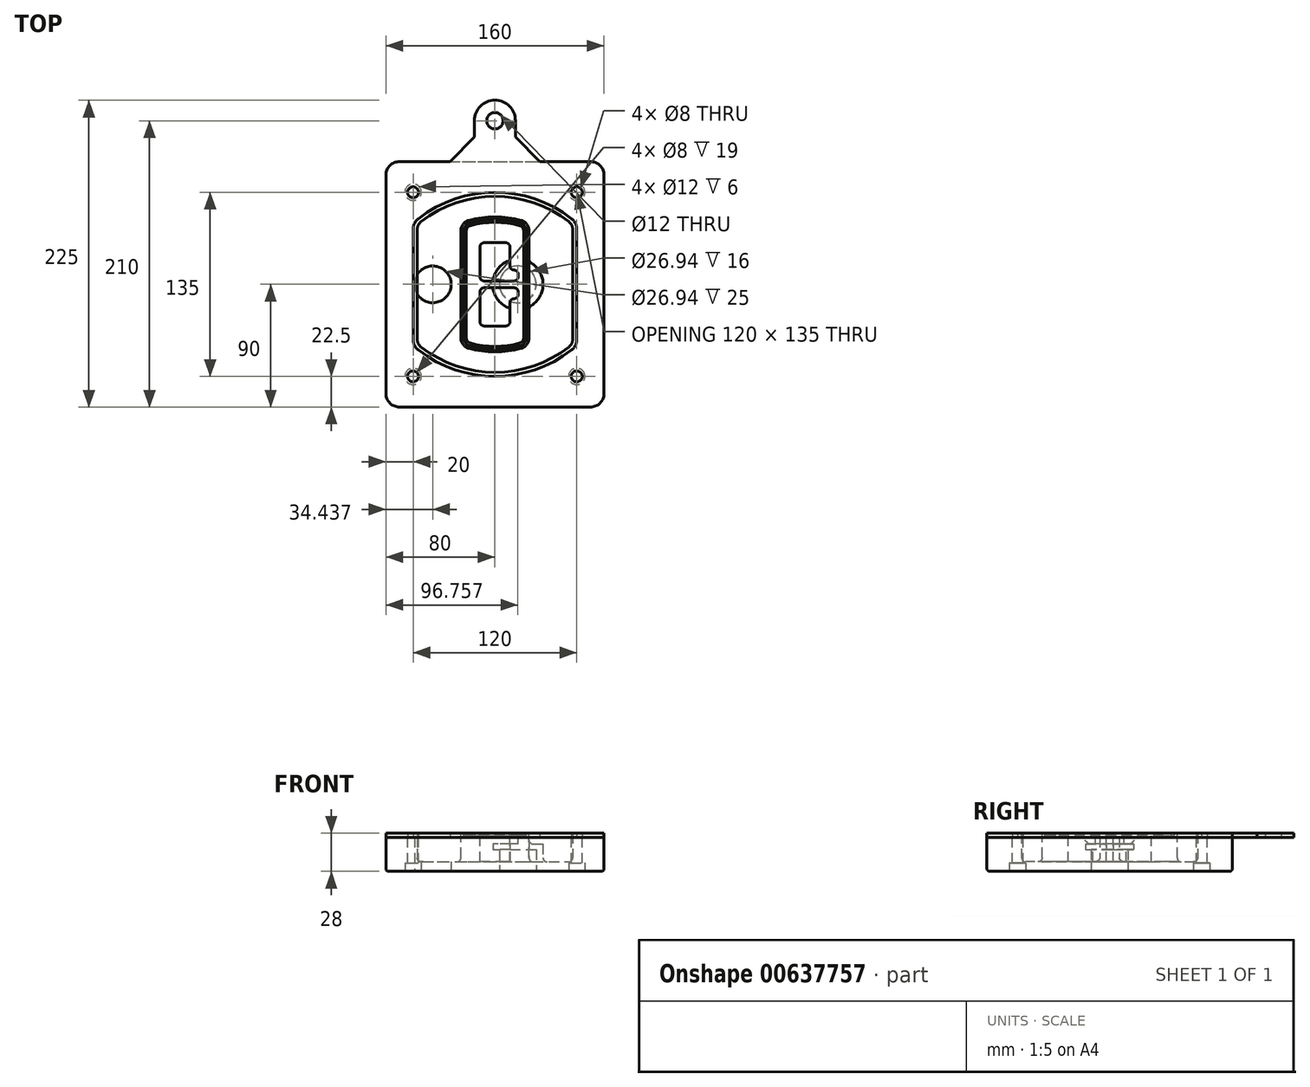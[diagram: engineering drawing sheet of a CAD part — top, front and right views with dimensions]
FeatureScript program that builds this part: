
annotation { "Feature Type Name" : "Feature", "Feature Type Description" : "" }
export const myFeature = defineFeature(function(context is Context, id is Id, definition is map)
    precondition{}
    {
        {
            var Q0;
            Q0=qCreatedBy(makeId("Top.planeOp"),FACE);
            var sketch = newSketch(context, id + "F0", { "sketchPlane" : qUnion([Q0])});
            skPoint(sketch, "E0.rect.middle", {"position": v(0, 0) * mm});
            skLineSegment(sketch, "E1.bottom", {"start": v(-70, -90) * mm, "end": v(70, -90) * mm});
            skLineSegment(sketch, "E1.top", {"start": v(-70, 90) * mm, "end": v(70, 90) * mm});
            skLineSegment(sketch, "E1.left", {"start": v(-80, -80) * mm, "end": v(-80, 80) * mm});
            skLineSegment(sketch, "E1.right", {"start": v(80, -80) * mm, "end": v(80, 80) * mm});
            skLineSegment(sketch, "E2", {"start": v(-80, 90) * mm, "end": v(80, -90) * mm, "construction": true});
            skLineSegment(sketch, "E3", {"start": v(80, 90) * mm, "end": v(-80, -90) * mm, "construction": true});
            skCircle(sketch, "E4", {"center": v(-60, 67.5) * mm, "radius": 4 * mm});
            skCircle(sketch, "E5", {"center": v(60, 67.5) * mm, "radius": 4 * mm});
            skCircle(sketch, "E6", {"center": v(60, -67.5) * mm, "radius": 4 * mm});
            skCircle(sketch, "E7", {"center": v(-60, -67.5) * mm, "radius": 4 * mm});
            skLineSegment(sketch, "E8", {"start": v(-60, 67.5) * mm, "end": v(60, 67.5) * mm, "construction": true});
            skLineSegment(sketch, "E9", {"start": v(60, 67.5) * mm, "end": v(60, -67.5) * mm, "construction": true});
            skLineSegment(sketch, "E10", {"start": v(60, -67.5) * mm, "end": v(-60, -67.5) * mm, "construction": true});
            skLineSegment(sketch, "E11", {"start": v(-60, -67.5) * mm, "end": v(-60, 67.5) * mm, "construction": true});
            skLineSegment(sketch, "E12", {"start": v(-60, 40.3) * mm, "end": v(-60, -40.3) * mm});
            skLineSegment(sketch, "E13", {"start": v(60, 40.3) * mm, "end": v(60, -40.3) * mm});
            skArc(sketch, "E14", {"start": v(56.15, 48.18) * mm, "mid": v(0, 67.5) * mm, "end": v(-56.15, 48.18) * mm});
            skArc(sketch, "E15", {"start": v(-56.15, -48.18) * mm, "mid": v(0, -67.5) * mm, "end": v(56.15, -48.18) * mm});
            skLineSegment(sketch, "E16", {"start": v(-60, 0) * mm, "end": v(60, 0) * mm, "construction": true});
            skPoint(sketch, "E17.visualSharp", {"position": v(-60, -45) * mm});
            skArc(sketch, "E17.filletArc", {"start": v(-60, -40.3) * mm, "mid": v(-58.99, -44.68) * mm, "end": v(-56.15, -48.18) * mm});
            skPoint(sketch, "E18.visualSharp", {"position": v(-60, 45) * mm});
            skArc(sketch, "E18.filletArc", {"start": v(-56.15, 48.18) * mm, "mid": v(-58.99, 44.68) * mm, "end": v(-60, 40.3) * mm});
            skPoint(sketch, "E19.visualSharp", {"position": v(60, 45) * mm});
            skArc(sketch, "E19.filletArc", {"start": v(60, 40.3) * mm, "mid": v(58.99, 44.68) * mm, "end": v(56.15, 48.18) * mm});
            skPoint(sketch, "E20.visualSharp", {"position": v(60, -45) * mm});
            skArc(sketch, "E20.filletArc", {"start": v(56.15, -48.18) * mm, "mid": v(58.99, -44.68) * mm, "end": v(60, -40.3) * mm});
            skPoint(sketch, "E21.visualSharp", {"position": v(-80, 90) * mm});
            skArc(sketch, "E21.filletArc", {"start": v(-70, 90) * mm, "mid": v(-77.07, 87.07) * mm, "end": v(-80, 80) * mm});
            skPoint(sketch, "E22.visualSharp", {"position": v(80, 90) * mm});
            skArc(sketch, "E22.filletArc", {"start": v(80, 80) * mm, "mid": v(77.07, 87.07) * mm, "end": v(70, 90) * mm});
            skPoint(sketch, "E23.visualSharp", {"position": v(80, -90) * mm});
            skArc(sketch, "E23.filletArc", {"start": v(70, -90) * mm, "mid": v(77.07, -87.07) * mm, "end": v(80, -80) * mm});
            skPoint(sketch, "E24.visualSharp", {"position": v(-80, -90) * mm});
            skArc(sketch, "E24.filletArc", {"start": v(-80, -80) * mm, "mid": v(-77.07, -87.07) * mm, "end": v(-70, -90) * mm});
            skArc(sketch, "E25.0", {"start": v(57, 40.3) * mm, "mid": v(56.3, 43.36) * mm, "end": v(54.3, 45.81) * mm});
            skLineSegment(sketch, "E25.1", {"start": v(57, 40.3) * mm, "end": v(57, -40.3) * mm});
            skArc(sketch, "E25.2", {"start": v(54.3, -45.81) * mm, "mid": v(56.3, -43.36) * mm, "end": v(57, -40.3) * mm});
            skArc(sketch, "E25.3", {"start": v(-54.3, -45.81) * mm, "mid": v(0, -64.5) * mm, "end": v(54.3, -45.81) * mm});
            skArc(sketch, "E25.4", {"start": v(-57, -40.3) * mm, "mid": v(-56.3, -43.36) * mm, "end": v(-54.3, -45.81) * mm});
            skArc(sketch, "E25.5", {"start": v(54.3, 45.81) * mm, "mid": v(0, 64.5) * mm, "end": v(-54.3, 45.81) * mm});
            skLineSegment(sketch, "E25.6", {"start": v(-57, 40.3) * mm, "end": v(-57, -40.3) * mm});
            skArc(sketch, "E25.7", {"start": v(-54.3, 45.81) * mm, "mid": v(-56.3, 43.36) * mm, "end": v(-57, 40.3) * mm});
            skArc(sketch, "E26.0", {"start": v(-58.62, 51.33) * mm, "mid": v(-62.58, 46.43) * mm, "end": v(-64, 40.3) * mm});
            skArc(sketch, "E26.1", {"start": v(58.62, 51.33) * mm, "mid": v(0, 71.5) * mm, "end": v(-58.62, 51.33) * mm});
            skArc(sketch, "E26.2", {"start": v(64, 40.3) * mm, "mid": v(62.58, 46.43) * mm, "end": v(58.62, 51.33) * mm});
            skLineSegment(sketch, "E26.3", {"start": v(64, 40.3) * mm, "end": v(64, -40.3) * mm});
            skArc(sketch, "E26.4", {"start": v(58.62, -51.33) * mm, "mid": v(62.58, -46.43) * mm, "end": v(64, -40.3) * mm});
            skLineSegment(sketch, "E26.5", {"start": v(-64, 40.3) * mm, "end": v(-64, -40.3) * mm});
            skArc(sketch, "E26.6", {"start": v(-58.62, -51.33) * mm, "mid": v(0, -71.5) * mm, "end": v(58.62, -51.33) * mm});
            skArc(sketch, "E26.7", {"start": v(-64, -40.3) * mm, "mid": v(-62.58, -46.43) * mm, "end": v(-58.62, -51.33) * mm});
            skSolve(sketch);
        }
        {
            var Q0;
            Q0=makeQuery(id+"F0.imprint","IMPRINT",FACE,{"disambiguationData":[TD([[makeQuery(id+"F0.imprint","IMPRINT",EDGE,{"derivedFrom":sQuery(id+"F0.wireOp",EDGE,"E1.bottom")}),1.0]])]});
            var Q1;
            Q1=makeQuery(id+"F0.imprint","IMPRINT",FACE,{"disambiguationData":[TD([[makeQuery(id+"F0.imprint","IMPRINT",EDGE,{"derivedFrom":sQuery(id+"F0.wireOp",EDGE,"E12")}),1.0]])]});
            var Q2;
            Q2=makeQuery(id+"F0.imprint","IMPRINT",FACE,{"disambiguationData":[TD([[makeQuery(id+"F0.imprint","IMPRINT",EDGE,{"derivedFrom":sQuery(id+"F0.wireOp",EDGE,"E25.0")}),1.0]])]});
            var Q3;
            Q3=makeQuery(id+"F0.imprint","IMPRINT",FACE,{"disambiguationData":[TD([[makeQuery(id+"F0.imprint","IMPRINT",EDGE,{"derivedFrom":sQuery(id+"F0.wireOp",EDGE,"E12")}),-1.0]])]});
            extrude(context, id + "F1", {"entities" : qUnion([Q0, Q1, Q2, Q3]), "oppositeDirection" : true, "depth" : 25 * mm});
        }
        {
            var Q0;
            Q0=makeQuery(id+"F0.imprint","IMPRINT",FACE,{"disambiguationData":[TD([[makeQuery(id+"F0.imprint","IMPRINT",EDGE,{"derivedFrom":sQuery(id+"F0.wireOp",EDGE,"E12")}),1.0]])]});
            extrude(context, id + "F2", {"entities" : qUnion([Q0]), "operationType" : NewBodyOperationType.ADD, "depth" : 3 * mm});
        }
        {
            var Q0;
            Q0=makeQuery(id+"F0.imprint","IMPRINT",FACE,{"disambiguationData":[TD([[makeQuery(id+"F0.imprint","IMPRINT",EDGE,{"derivedFrom":sQuery(id+"F0.wireOp",EDGE,"E25.0")}),1.0]])]});
            extrude(context, id + "F3", {"entities" : qUnion([Q0]), "operationType" : NewBodyOperationType.REMOVE, "oppositeDirection" : true, "depth" : 18 * mm});
        }
        {
            var Q0;
            Q0=makeQuery(id+"F2.opExtrude","CAP_FACE",FACE,{"disambiguationData":[OSD([sQuery(id+"F0.wireOp",EDGE,"E12"),sQuery(id+"F0.wireOp",EDGE,"E13"),sQuery(id+"F0.wireOp",EDGE,"E14"),sQuery(id+"F0.wireOp",EDGE,"E15"),sQuery(id+"F0.wireOp",EDGE,"E17.filletArc"),sQuery(id+"F0.wireOp",EDGE,"E18.filletArc"),sQuery(id+"F0.wireOp",EDGE,"E19.filletArc"),sQuery(id+"F0.wireOp",EDGE,"E20.filletArc"),sQuery(id+"F0.wireOp",EDGE,"E25.0"),sQuery(id+"F0.wireOp",EDGE,"E25.1"),sQuery(id+"F0.wireOp",EDGE,"E25.2"),sQuery(id+"F0.wireOp",EDGE,"E25.3"),sQuery(id+"F0.wireOp",EDGE,"E25.4"),sQuery(id+"F0.wireOp",EDGE,"E25.5"),sQuery(id+"F0.wireOp",EDGE,"E25.6"),sQuery(id+"F0.wireOp",EDGE,"E25.7")])],"isStart":false});
            var sketch = newSketch(context, id + "F4", { "sketchPlane" : qUnion([Q0])});
            skArc(sketch, "E27.0", {"start": v(-19.08, -46.97) * mm, "mid": v(0, -49.5) * mm, "end": v(19.08, -46.97) * mm});
            skArc(sketch, "E28.0", {"start": v(19.08, 46.97) * mm, "mid": v(0, 49.5) * mm, "end": v(-19.08, 46.97) * mm});
            skLineSegment(sketch, "E29", {"start": v(-25, 39.25) * mm, "end": v(-25, -39.25) * mm});
            skLineSegment(sketch, "E30", {"start": v(25, 39.25) * mm, "end": v(25, -39.25) * mm});
            skLineSegment(sketch, "E31", {"start": v(-25, 45.1) * mm, "end": v(25, 45.1) * mm, "construction": true});
            skLineSegment(sketch, "E32", {"start": v(-25, -45.1) * mm, "end": v(25, -45.1) * mm, "construction": true});
            skPoint(sketch, "E33.visualSharp", {"position": v(-25, 45.1) * mm});
            skArc(sketch, "E33.filletArc", {"start": v(-19.08, 46.97) * mm, "mid": v(-23.35, 44.11) * mm, "end": v(-25, 39.25) * mm});
            skPoint(sketch, "E34.visualSharp", {"position": v(25, 45.1) * mm});
            skArc(sketch, "E34.filletArc", {"start": v(25, 39.25) * mm, "mid": v(23.35, 44.11) * mm, "end": v(19.08, 46.97) * mm});
            skPoint(sketch, "E35.visualSharp", {"position": v(25, -45.1) * mm});
            skArc(sketch, "E35.filletArc", {"start": v(19.08, -46.97) * mm, "mid": v(23.35, -44.11) * mm, "end": v(25, -39.25) * mm});
            skPoint(sketch, "E36.visualSharp", {"position": v(-25, -45.1) * mm});
            skArc(sketch, "E36.filletArc", {"start": v(-25, -39.25) * mm, "mid": v(-23.35, -44.11) * mm, "end": v(-19.08, -46.97) * mm});
            skArc(sketch, "E37.0", {"start": v(54.3, 45.81) * mm, "mid": v(0, 64.5) * mm, "end": v(-54.3, 45.81) * mm});
            skArc(sketch, "E37.1", {"start": v(-54.3, 45.81) * mm, "mid": v(-56.3, 43.36) * mm, "end": v(-57, 40.3) * mm});
            skLineSegment(sketch, "E37.2", {"start": v(-57, 40.3) * mm, "end": v(-57, -40.3) * mm});
            skArc(sketch, "E37.3", {"start": v(-57, -40.3) * mm, "mid": v(-56.3, -43.36) * mm, "end": v(-54.3, -45.81) * mm});
            skArc(sketch, "E37.4", {"start": v(-54.3, -45.81) * mm, "mid": v(0, -64.5) * mm, "end": v(54.3, -45.81) * mm});
            skArc(sketch, "E37.5", {"start": v(54.3, -45.81) * mm, "mid": v(56.3, -43.36) * mm, "end": v(57, -40.3) * mm});
            skLineSegment(sketch, "E37.6", {"start": v(57, 40.3) * mm, "end": v(57, -40.3) * mm});
            skArc(sketch, "E37.7", {"start": v(57, 40.3) * mm, "mid": v(56.3, 43.36) * mm, "end": v(54.3, 45.81) * mm});
            skLineSegment(sketch, "E38.0", {"start": v(23, 39.25) * mm, "end": v(23, -39.25) * mm});
            skArc(sketch, "E38.1", {"start": v(18.56, -45.04) * mm, "mid": v(21.76, -42.9) * mm, "end": v(23, -39.25) * mm});
            skArc(sketch, "E38.2", {"start": v(-18.56, -45.04) * mm, "mid": v(0, -47.5) * mm, "end": v(18.56, -45.04) * mm});
            skArc(sketch, "E38.3", {"start": v(-23, -39.25) * mm, "mid": v(-21.76, -42.9) * mm, "end": v(-18.56, -45.04) * mm});
            skLineSegment(sketch, "E38.4", {"start": v(-23, 39.25) * mm, "end": v(-23, -39.25) * mm});
            skArc(sketch, "E38.5", {"start": v(23, 39.25) * mm, "mid": v(21.76, 42.9) * mm, "end": v(18.56, 45.04) * mm});
            skArc(sketch, "E38.6", {"start": v(-18.56, 45.04) * mm, "mid": v(-21.76, 42.9) * mm, "end": v(-23, 39.25) * mm});
            skArc(sketch, "E38.7", {"start": v(18.56, 45.04) * mm, "mid": v(0, 47.5) * mm, "end": v(-18.56, 45.04) * mm});
            skArc(sketch, "E39.0", {"start": v(21, 39.25) * mm, "mid": v(20.18, 41.68) * mm, "end": v(18.04, 43.1) * mm});
            skLineSegment(sketch, "E39.1", {"start": v(21, 39.25) * mm, "end": v(21, -39.25) * mm});
            skArc(sketch, "E39.2", {"start": v(18.04, -43.1) * mm, "mid": v(20.18, -41.68) * mm, "end": v(21, -39.25) * mm});
            skArc(sketch, "E39.3", {"start": v(-18.04, -43.1) * mm, "mid": v(0, -45.5) * mm, "end": v(18.04, -43.1) * mm});
            skArc(sketch, "E39.4", {"start": v(-21, -39.25) * mm, "mid": v(-20.18, -41.68) * mm, "end": v(-18.04, -43.1) * mm});
            skArc(sketch, "E39.5", {"start": v(18.04, 43.1) * mm, "mid": v(0, 45.5) * mm, "end": v(-18.04, 43.1) * mm});
            skLineSegment(sketch, "E39.6", {"start": v(-21, 39.25) * mm, "end": v(-21, -39.25) * mm});
            skArc(sketch, "E39.7", {"start": v(-18.04, 43.1) * mm, "mid": v(-20.18, 41.68) * mm, "end": v(-21, 39.25) * mm});
            skLineSegment(sketch, "E40", {"start": v(-25, 0) * mm, "end": v(25, 0) * mm, "construction": true});
            skLineSegment(sketch, "E41", {"start": v(-11, 5.5) * mm, "end": v(-11, 27.5) * mm});
            skLineSegment(sketch, "E42", {"start": v(-8, 30.5) * mm, "end": v(8, 30.5) * mm});
            skLineSegment(sketch, "E43", {"start": v(11, 27.5) * mm, "end": v(11, 13.5) * mm});
            skLineSegment(sketch, "E44", {"start": v(14, 10.5) * mm, "end": v(14, 10.5) * mm});
            skLineSegment(sketch, "E45", {"start": v(17, 7.5) * mm, "end": v(17, 5.5) * mm});
            skLineSegment(sketch, "E46", {"start": v(14, 2.5) * mm, "end": v(-8, 2.5) * mm});
            skPoint(sketch, "E47.visualSharp", {"position": v(-11, 30.5) * mm});
            skArc(sketch, "E47.filletArc", {"start": v(-8, 30.5) * mm, "mid": v(-10.12, 29.62) * mm, "end": v(-11, 27.5) * mm});
            skPoint(sketch, "E48.visualSharp", {"position": v(11, 30.5) * mm});
            skArc(sketch, "E48.filletArc", {"start": v(11, 27.5) * mm, "mid": v(10.12, 29.62) * mm, "end": v(8, 30.5) * mm});
            skPoint(sketch, "E49.visualSharp", {"position": v(11, 10.5) * mm});
            skArc(sketch, "E49.filletArc", {"start": v(11, 13.5) * mm, "mid": v(11.88, 11.38) * mm, "end": v(14, 10.5) * mm});
            skPoint(sketch, "E50.visualSharp", {"position": v(17, 10.5) * mm});
            skArc(sketch, "E50.filletArc", {"start": v(17, 7.5) * mm, "mid": v(16.12, 9.62) * mm, "end": v(14, 10.5) * mm});
            skPoint(sketch, "E51.visualSharp", {"position": v(17, 2.5) * mm});
            skArc(sketch, "E51.filletArc", {"start": v(14, 2.5) * mm, "mid": v(16.12, 3.38) * mm, "end": v(17, 5.5) * mm});
            skPoint(sketch, "E52.visualSharp", {"position": v(-11, 2.5) * mm});
            skArc(sketch, "E52.filletArc", {"start": v(-11, 5.5) * mm, "mid": v(-10.12, 3.38) * mm, "end": v(-8, 2.5) * mm});
            skLineSegment(sketch, "E53.0.MirrorCS", {"start": v(14, -2.5) * mm, "end": v(-8, -2.5) * mm});
            skArc(sketch, "E54.0.MirrorCS", {"start": v(-11, -5.5) * mm, "mid": v(-10.12, -3.38) * mm, "end": v(-8, -2.5) * mm});
            skLineSegment(sketch, "E55.0.MirrorCS", {"start": v(-11, -5.5) * mm, "end": v(-11, -27.5) * mm});
            skArc(sketch, "E56.0.MirrorCS", {"start": v(-8, -30.5) * mm, "mid": v(-10.12, -29.62) * mm, "end": v(-11, -27.5) * mm});
            skLineSegment(sketch, "E57.0.MirrorCS", {"start": v(-8, -30.5) * mm, "end": v(8, -30.5) * mm});
            skArc(sketch, "E58.0.MirrorCS", {"start": v(11, -27.5) * mm, "mid": v(10.12, -29.62) * mm, "end": v(8, -30.5) * mm});
            skLineSegment(sketch, "E59.0.MirrorCS", {"start": v(11, -27.5) * mm, "end": v(11, -13.5) * mm});
            skArc(sketch, "E60.0.MirrorCS", {"start": v(11, -13.5) * mm, "mid": v(11.88, -11.38) * mm, "end": v(14, -10.5) * mm});
            skArc(sketch, "E61.0.MirrorCS", {"start": v(17, -7.5) * mm, "mid": v(16.12, -9.62) * mm, "end": v(14, -10.5) * mm});
            skLineSegment(sketch, "E62.0.MirrorCS", {"start": v(17, -7.5) * mm, "end": v(17, -5.5) * mm});
            skArc(sketch, "E63.0.MirrorCS", {"start": v(14, -2.5) * mm, "mid": v(16.12, -3.38) * mm, "end": v(17, -5.5) * mm});
            skSolve(sketch);
        }
        {
            var Q0;
            Q0=makeQuery(id+"F4.imprint","IMPRINT",FACE,{"disambiguationData":[TD([[makeQuery(id+"F4.imprint","IMPRINT",EDGE,{"derivedFrom":sQuery(id+"F4.wireOp",EDGE,"E27.0")}),1.0]])]});
            var Q1;
            Q1=makeQuery(id+"F4.imprint","IMPRINT",FACE,{"disambiguationData":[TD([[makeQuery(id+"F4.imprint","IMPRINT",EDGE,{"derivedFrom":sQuery(id+"F4.wireOp",EDGE,"E38.0")}),-1.0]])]});
            var Q2;
            Q2=makeQuery(id+"F4.imprint","IMPRINT",FACE,{"disambiguationData":[TD([[makeQuery(id+"F4.imprint","IMPRINT",EDGE,{"derivedFrom":sQuery(id+"F4.wireOp",EDGE,"E39.0")}),1.0]])]});
            extrude(context, id + "F5", {"entities" : qUnion([Q0, Q1, Q2]), "operationType" : NewBodyOperationType.ADD, "endBound" : BoundingType.UP_TO_NEXT, "oppositeDirection" : true, "depth" : 25 * mm});
        }
        {
            var Q0;
            Q0=makeQuery(id+"F4.imprint","IMPRINT",FACE,{"disambiguationData":[TD([[makeQuery(id+"F4.imprint","IMPRINT",EDGE,{"derivedFrom":sQuery(id+"F4.wireOp",EDGE,"E38.0")}),-1.0]])]});
            extrude(context, id + "F6", {"entities" : qUnion([Q0]), "operationType" : NewBodyOperationType.REMOVE, "oppositeDirection" : true, "depth" : 2 * mm});
        }
        {
            var Q0;
            Q0=makeQuery(id+"F1.opExtrude","CAP_FACE",FACE,{"disambiguationData":[OSD([sQuery(id+"F0.wireOp",EDGE,"E1.bottom"),sQuery(id+"F0.wireOp",EDGE,"E1.top"),sQuery(id+"F0.wireOp",EDGE,"E1.left"),sQuery(id+"F0.wireOp",EDGE,"E1.right"),sQuery(id+"F0.wireOp",EDGE,"E4"),sQuery(id+"F0.wireOp",EDGE,"E5"),sQuery(id+"F0.wireOp",EDGE,"E6"),sQuery(id+"F0.wireOp",EDGE,"E7"),sQuery(id+"F0.wireOp",EDGE,"E21.filletArc"),sQuery(id+"F0.wireOp",EDGE,"E22.filletArc"),sQuery(id+"F0.wireOp",EDGE,"E23.filletArc"),sQuery(id+"F0.wireOp",EDGE,"E24.filletArc")])],"isStart":false});
            var sketch = newSketch(context, id + "F7", { "sketchPlane" : qUnion([Q0])});
            skCircle(sketch, "E64", {"center": v(16.76, 0) * mm, "radius": 13.47 * mm});
            skCircle(sketch, "E65", {"center": v(-45.56, 0) * mm, "radius": 13.47 * mm});
            skLineSegment(sketch, "E66", {"start": v(80, 0) * mm, "end": v(-80, 0) * mm});
            skCircle(sketch, "E67", {"center": v(16.76, 0) * mm, "radius": 18.47 * mm});
            skCircle(sketch, "E68", {"center": v(60, -67.5) * mm, "radius": 6 * mm});
            skCircle(sketch, "E69", {"center": v(-60, -67.5) * mm, "radius": 6 * mm});
            skCircle(sketch, "E70", {"center": v(-60, 67.5) * mm, "radius": 6 * mm});
            skCircle(sketch, "E71", {"center": v(60, 67.5) * mm, "radius": 6 * mm});
            skSolve(sketch);
        }
        {
            var Q0;
            {var subQ1=sQuery(id+"F7.wireOp",EDGE,"E66");var subQ4=sQuery(id+"F7.wireOp",EDGE,"E64");var subQ6=makeQuery(id+"F7.imprint","INTERSECT",VERTEX,{"disambiguationData":[OD(0.0)],"derivedFrom":[subQ4,subQ1]});Q0=makeQuery(id+"F7.imprint","IMPRINT",FACE,{"disambiguationData":[TD([[makeQuery(id+"F7.imprint","IMPRINT",EDGE,{"disambiguationData":[TD([[subQ6,-1.0]])],"derivedFrom":subQ4}),-1.0]])]});}
            var Q1;
            {var subQ0=sQuery(id+"F7.wireOp",EDGE,"E66");var subQ1=sQuery(id+"F7.wireOp",EDGE,"E64");var subQ3=makeQuery(id+"F7.imprint","INTERSECT",VERTEX,{"disambiguationData":[OD(0.0)],"derivedFrom":[subQ1,subQ0]});Q1=makeQuery(id+"F7.imprint","IMPRINT",FACE,{"disambiguationData":[TD([[makeQuery(id+"F7.imprint","IMPRINT",EDGE,{"disambiguationData":[TD([[subQ3,-1.0]])],"derivedFrom":subQ1}),1.0]])]});}
            var Q2;
            {var subQ0=sQuery(id+"F7.wireOp",EDGE,"E66");var subQ1=sQuery(id+"F7.wireOp",EDGE,"E64");var subQ3=makeQuery(id+"F7.imprint","INTERSECT",VERTEX,{"disambiguationData":[OD(0.0)],"derivedFrom":[subQ1,subQ0]});Q2=makeQuery(id+"F7.imprint","IMPRINT",FACE,{"disambiguationData":[TD([[makeQuery(id+"F7.imprint","IMPRINT",EDGE,{"disambiguationData":[TD([[subQ3,1.0]])],"derivedFrom":subQ1}),1.0]])]});}
            var Q3;
            {var subQ1=sQuery(id+"F7.wireOp",EDGE,"E66");var subQ4=sQuery(id+"F7.wireOp",EDGE,"E64");var subQ6=makeQuery(id+"F7.imprint","INTERSECT",VERTEX,{"disambiguationData":[OD(0.0)],"derivedFrom":[subQ4,subQ1]});Q3=makeQuery(id+"F7.imprint","IMPRINT",FACE,{"disambiguationData":[TD([[makeQuery(id+"F7.imprint","IMPRINT",EDGE,{"disambiguationData":[TD([[subQ6,1.0]])],"derivedFrom":subQ4}),-1.0]])]});}
            extrude(context, id + "F8", {"entities" : qUnion([Q0, Q1, Q2, Q3]), "operationType" : NewBodyOperationType.ADD, "oppositeDirection" : true, "depth" : 20 * mm});
        }
        {
            var Q0;
            {var subQ0=sQuery(id+"F7.wireOp",EDGE,"E66");var subQ1=sQuery(id+"F7.wireOp",EDGE,"E64");var subQ3=makeQuery(id+"F7.imprint","INTERSECT",VERTEX,{"disambiguationData":[OD(0.0)],"derivedFrom":[subQ1,subQ0]});Q0=makeQuery(id+"F7.imprint","IMPRINT",FACE,{"disambiguationData":[TD([[makeQuery(id+"F7.imprint","IMPRINT",EDGE,{"disambiguationData":[TD([[subQ3,-1.0]])],"derivedFrom":subQ1}),1.0]])]});}
            var Q1;
            {var subQ0=sQuery(id+"F7.wireOp",EDGE,"E66");var subQ1=sQuery(id+"F7.wireOp",EDGE,"E64");var subQ3=makeQuery(id+"F7.imprint","INTERSECT",VERTEX,{"disambiguationData":[OD(0.0)],"derivedFrom":[subQ1,subQ0]});Q1=makeQuery(id+"F7.imprint","IMPRINT",FACE,{"disambiguationData":[TD([[makeQuery(id+"F7.imprint","IMPRINT",EDGE,{"disambiguationData":[TD([[subQ3,1.0]])],"derivedFrom":subQ1}),1.0]])]});}
            extrude(context, id + "F9", {"entities" : qUnion([Q0, Q1]), "operationType" : NewBodyOperationType.REMOVE, "oppositeDirection" : true, "depth" : 16 * mm});
        }
        {
            var Q0;
            {var subQ0=sQuery(id+"F7.wireOp",EDGE,"E66");var subQ1=sQuery(id+"F7.wireOp",EDGE,"E65");var subQ3=makeQuery(id+"F7.imprint","INTERSECT",VERTEX,{"disambiguationData":[OD(0.0)],"derivedFrom":[subQ1,subQ0]});Q0=makeQuery(id+"F7.imprint","IMPRINT",FACE,{"disambiguationData":[TD([[makeQuery(id+"F7.imprint","IMPRINT",EDGE,{"disambiguationData":[TD([[subQ3,-1.0]])],"derivedFrom":subQ1}),1.0]])]});}
            var Q1;
            {var subQ0=sQuery(id+"F7.wireOp",EDGE,"E66");var subQ1=sQuery(id+"F7.wireOp",EDGE,"E65");var subQ3=makeQuery(id+"F7.imprint","INTERSECT",VERTEX,{"disambiguationData":[OD(0.0)],"derivedFrom":[subQ1,subQ0]});Q1=makeQuery(id+"F7.imprint","IMPRINT",FACE,{"disambiguationData":[TD([[makeQuery(id+"F7.imprint","IMPRINT",EDGE,{"disambiguationData":[TD([[subQ3,1.0]])],"derivedFrom":subQ1}),1.0]])]});}
            extrude(context, id + "F10", {"entities" : qUnion([Q0, Q1]), "operationType" : NewBodyOperationType.REMOVE, "oppositeDirection" : true, "depth" : 25 * mm});
        }
        {
            var Q0;
            Q0=makeQuery(id+"F7.imprint","IMPRINT",FACE,{"disambiguationData":[TD([[makeQuery(id+"F7.imprint","IMPRINT",EDGE,{"derivedFrom":sQuery(id+"F7.wireOp",EDGE,"E68")}),1.0]])]});
            var Q1;
            Q1=makeQuery(id+"F7.imprint","IMPRINT",FACE,{"disambiguationData":[TD([[makeQuery(id+"F7.imprint","IMPRINT",EDGE,{"derivedFrom":makeQuery(id+"F1.opExtrude","CAP_EDGE",EDGE,{"disambiguationData":[OSD([sQuery(id+"F0.wireOp",EDGE,"E5")])],"isStart":false})}),-1.0]])]});
            var Q2;
            Q2=makeQuery(id+"F7.imprint","IMPRINT",FACE,{"disambiguationData":[TD([[makeQuery(id+"F7.imprint","IMPRINT",EDGE,{"derivedFrom":sQuery(id+"F7.wireOp",EDGE,"E69")}),1.0]])]});
            var Q3;
            Q3=makeQuery(id+"F7.imprint","IMPRINT",FACE,{"disambiguationData":[TD([[makeQuery(id+"F7.imprint","IMPRINT",EDGE,{"derivedFrom":makeQuery(id+"F1.opExtrude","CAP_EDGE",EDGE,{"disambiguationData":[OSD([sQuery(id+"F0.wireOp",EDGE,"E4")])],"isStart":false})}),-1.0]])]});
            var Q4;
            Q4=makeQuery(id+"F7.imprint","IMPRINT",FACE,{"disambiguationData":[TD([[makeQuery(id+"F7.imprint","IMPRINT",EDGE,{"derivedFrom":sQuery(id+"F7.wireOp",EDGE,"E70")}),1.0]])]});
            var Q5;
            Q5=makeQuery(id+"F7.imprint","IMPRINT",FACE,{"disambiguationData":[TD([[makeQuery(id+"F7.imprint","IMPRINT",EDGE,{"derivedFrom":makeQuery(id+"F1.opExtrude","CAP_EDGE",EDGE,{"disambiguationData":[OSD([sQuery(id+"F0.wireOp",EDGE,"E7")])],"isStart":false})}),-1.0]])]});
            var Q6;
            Q6=makeQuery(id+"F7.imprint","IMPRINT",FACE,{"disambiguationData":[TD([[makeQuery(id+"F7.imprint","IMPRINT",EDGE,{"derivedFrom":sQuery(id+"F7.wireOp",EDGE,"E71")}),1.0]])]});
            var Q7;
            Q7=makeQuery(id+"F7.imprint","IMPRINT",FACE,{"disambiguationData":[TD([[makeQuery(id+"F7.imprint","IMPRINT",EDGE,{"derivedFrom":makeQuery(id+"F1.opExtrude","CAP_EDGE",EDGE,{"disambiguationData":[OSD([sQuery(id+"F0.wireOp",EDGE,"E6")])],"isStart":false})}),-1.0]])]});
            extrude(context, id + "F11", {"entities" : qUnion([Q0, Q1, Q2, Q3, Q4, Q5, Q6, Q7]), "operationType" : NewBodyOperationType.REMOVE, "oppositeDirection" : true, "depth" : 6 * mm});
        }
        {
            var Q0;
            Q0=makeQuery(id+"F9.boolean.opBoolean","COPY",FACE,{"derivedFrom":makeQuery(id+"F9.opExtrude","CAP_FACE",FACE,{"disambiguationData":[OSD([sQuery(id+"F7.wireOp",EDGE,"E64")])],"isStart":false})});
            var sketch = newSketch(context, id + "F12", { "sketchPlane" : qUnion([Q0])});
            skArc(sketch, "E72.0", {"start": v(11, 17.55) * mm, "mid": v(2.57, 11.82) * mm, "end": v(-1.54, 2.5) * mm});
            skArc(sketch, "E72.1", {"start": v(-1.54, -2.5) * mm, "mid": v(2.57, -11.82) * mm, "end": v(11, -17.55) * mm});
            skLineSegment(sketch, "E73", {"start": v(-1.54, -2.5) * mm, "end": v(14, -2.5) * mm});
            skLineSegment(sketch, "E74.0", {"start": v(14, 2.5) * mm, "end": v(-1.54, 2.5) * mm});
            skArc(sketch, "E74.1", {"start": v(14, 2.5) * mm, "mid": v(16.12, 3.38) * mm, "end": v(17, 5.5) * mm});
            skLineSegment(sketch, "E74.2", {"start": v(17, 7.5) * mm, "end": v(17, 5.5) * mm});
            skArc(sketch, "E74.3", {"start": v(17, 7.5) * mm, "mid": v(16.12, 9.62) * mm, "end": v(14, 10.5) * mm});
            skArc(sketch, "E74.4", {"start": v(11, 13.5) * mm, "mid": v(11.88, 11.38) * mm, "end": v(14, 10.5) * mm});
            skLineSegment(sketch, "E74.5", {"start": v(11, 17.55) * mm, "end": v(11, 13.5) * mm});
            skLineSegment(sketch, "E74.7", {"start": v(14, -2.5) * mm, "end": v(-1.54, -2.5) * mm});
            skArc(sketch, "E74.8", {"start": v(14, -2.5) * mm, "mid": v(16.12, -3.38) * mm, "end": v(17, -5.5) * mm});
            skLineSegment(sketch, "E74.9", {"start": v(17, -7.5) * mm, "end": v(17, -5.5) * mm});
            skArc(sketch, "E74.10", {"start": v(17, -7.5) * mm, "mid": v(16.12, -9.62) * mm, "end": v(14, -10.5) * mm});
            skArc(sketch, "E74.11", {"start": v(11, -13.5) * mm, "mid": v(11.88, -11.38) * mm, "end": v(14, -10.5) * mm});
            skLineSegment(sketch, "E74.12", {"start": v(11, -17.55) * mm, "end": v(11, -13.5) * mm});
            skPoint(sketch, "E75.orphan", {"position": v(11, -27.5) * mm});
            skPoint(sketch, "E76.orphan", {"position": v(-8, -2.5) * mm});
            skPoint(sketch, "E77.orphan", {"position": v(-8, 2.5) * mm});
            skPoint(sketch, "E78.orphan", {"position": v(11, 27.5) * mm});
            skSolve(sketch);
        }
        {
            var Q0;
            {var subQ7=sQuery(id+"F12.wireOp",EDGE,"E72.0");var subQ14=sQuery(id+"F12.wireOp",EDGE,"E72.1");var subQ16=sQuery(id+"F12.wireOp",EDGE,"E74.1");var subQ18=sQuery(id+"F12.wireOp",EDGE,"E74.8");Q0=qUnion([makeQuery(id+"F12.imprint","IMPRINT",FACE,{"disambiguationData":[TD([[makeQuery(id+"F12.imprint","IMPRINT",EDGE,{"derivedFrom":subQ7}),1.0]])]}),makeQuery(id+"F12.imprint","IMPRINT",FACE,{"disambiguationData":[TD([[makeQuery(id+"F12.imprint","IMPRINT",EDGE,{"derivedFrom":subQ14}),1.0]])]}),makeQuery(id+"F12.imprint","IMPRINT",FACE,{"disambiguationData":[TD([[makeQuery(id+"F12.imprint","IMPRINT",EDGE,{"derivedFrom":subQ16}),1.0]])]}),makeQuery(id+"F12.imprint","IMPRINT",FACE,{"disambiguationData":[TD([[makeQuery(id+"F12.imprint","IMPRINT",EDGE,{"derivedFrom":subQ18}),-1.0]])]})]);}
            var Q1;
            Q1=makeQuery(id+"F5.boolean.opBoolean","SPLIT",FACE,{"disambiguationData":[TD([makeQuery(id+"F5.opExtrude","SWEPT_FACE",FACE,{"disambiguationData":[OSD([sQuery(id+"F4.wireOp",EDGE,"E41")])]})])],"derivedFrom":makeQuery(id+"F3.boolean.opBoolean","COPY",FACE,{"derivedFrom":makeQuery(id+"F3.opExtrude","CAP_FACE",FACE,{"disambiguationData":[OSD([sQuery(id+"F0.wireOp",EDGE,"E25.0"),sQuery(id+"F0.wireOp",EDGE,"E25.1"),sQuery(id+"F0.wireOp",EDGE,"E25.2"),sQuery(id+"F0.wireOp",EDGE,"E25.3"),sQuery(id+"F0.wireOp",EDGE,"E25.4"),sQuery(id+"F0.wireOp",EDGE,"E25.5"),sQuery(id+"F0.wireOp",EDGE,"E25.6"),sQuery(id+"F0.wireOp",EDGE,"E25.7")])],"isStart":false})})});
            extrude(context, id + "F13", {"entities" : qUnion([Q0]), "operationType" : NewBodyOperationType.REMOVE, "endBound" : BoundingType.UP_TO_SURFACE, "endBoundEntityFace" : qUnion([Q1]), "depth" : 25 * mm});
        }
        {
            var Q0;
            Q0=makeQuery(id+"F3.boolean.opBoolean","COPY",EDGE,{"derivedFrom":makeQuery(id+"F3.opExtrude","CAP_EDGE",EDGE,{"disambiguationData":[OSD([sQuery(id+"F0.wireOp",EDGE,"E25.6")])],"isStart":false})});
            var Q1;
            Q1=makeQuery(id+"F8.boolean.opBoolean","INTERSECT",EDGE,{"derivedFrom":[makeQuery(id+"F5.opExtrude","SWEPT_FACE",FACE,{"disambiguationData":[OSD([sQuery(id+"F4.wireOp",EDGE,"E30")])]}),makeQuery(id+"F8.opExtrude","CAP_FACE",FACE,{"disambiguationData":[OSD([sQuery(id+"F7.wireOp",EDGE,"E67")])],"isStart":false})]});
            var Q2;
            Q2=makeQuery(id+"F8.boolean.opBoolean","INTERSECT",EDGE,{"disambiguationData":[OD(1.0)],"derivedFrom":[makeQuery(id+"F5.opExtrude","SWEPT_FACE",FACE,{"disambiguationData":[OSD([sQuery(id+"F4.wireOp",EDGE,"E30")])]}),makeQuery(id+"F8.opExtrude","SWEPT_FACE",FACE,{"disambiguationData":[OSD([sQuery(id+"F7.wireOp",EDGE,"E67")])]})]});
            var Q3;
            {var subQ0=sQuery(id+"F4.wireOp",EDGE,"E30");Q3=makeQuery(id+"F8.boolean.opBoolean","SPLIT",EDGE,{"disambiguationData":[TD([makeQuery(id+"F5.opExtrude","SWEPT_FACE",FACE,{"disambiguationData":[OSD([sQuery(id+"F4.wireOp",EDGE,"E35.filletArc")])]})])],"derivedFrom":makeQuery(id+"F5.opExtrude","CAP_EDGE",EDGE,{"disambiguationData":[OSD([subQ0])],"isStart":false})});}
            var Q4;
            {var subQ0=sQuery(id+"F0.wireOp",EDGE,"E25.7");var subQ1=sQuery(id+"F0.wireOp",EDGE,"E25.1");var subQ2=sQuery(id+"F0.wireOp",EDGE,"E25.6");var subQ3=sQuery(id+"F0.wireOp",EDGE,"E25.5");var subQ4=sQuery(id+"F0.wireOp",EDGE,"E25.4");var subQ5=sQuery(id+"F0.wireOp",EDGE,"E25.0");var subQ6=sQuery(id+"F0.wireOp",EDGE,"E25.2");var subQ7=sQuery(id+"F0.wireOp",EDGE,"E25.3");Q4=makeQuery(id+"F8.boolean.opBoolean","INTERSECT",EDGE,{"derivedFrom":[makeQuery(id+"F5.boolean.opBoolean","SPLIT",FACE,{"disambiguationData":[TD([makeQuery(id+"F2.opExtrude","SWEPT_FACE",FACE,{"disambiguationData":[OSD([subQ5])]})])],"derivedFrom":makeQuery(id+"F3.boolean.opBoolean","COPY",FACE,{"derivedFrom":makeQuery(id+"F3.opExtrude","CAP_FACE",FACE,{"disambiguationData":[OSD([subQ5,subQ1,subQ6,subQ7,subQ4,subQ3,subQ2,subQ0])],"isStart":false})})}),makeQuery(id+"F8.opExtrude","SWEPT_FACE",FACE,{"disambiguationData":[OSD([sQuery(id+"F7.wireOp",EDGE,"E67")])]})]});}
            var Q5;
            Q5=makeQuery(id+"F8.boolean.opBoolean","INTERSECT",EDGE,{"disambiguationData":[OD(0.0)],"derivedFrom":[makeQuery(id+"F5.opExtrude","SWEPT_FACE",FACE,{"disambiguationData":[OSD([sQuery(id+"F4.wireOp",EDGE,"E30")])]}),makeQuery(id+"F8.opExtrude","SWEPT_FACE",FACE,{"disambiguationData":[OSD([sQuery(id+"F7.wireOp",EDGE,"E67")])]})]});
            fillet(context, id + "F14", {"entities" : qUnion([Q0, Q1, Q2, Q3, Q4, Q5]), "radius" : 3 * mm, "tangentPropagation" : true, "allowEdgeOverflow" : false});
        }
        {
            var Q0;
            Q0=makeQuery(id+"F1.opExtrude","CAP_EDGE",EDGE,{"disambiguationData":[OSD([sQuery(id+"F0.wireOp",EDGE,"E1.bottom")])],"isStart":false});
            fillet(context, id + "F15", {"entities" : qUnion([Q0]), "radius" : 2 * mm, "tangentPropagation" : true, "allowEdgeOverflow" : false});
        }
        {
            var Q0;
            {var subQ0=sQuery(id+"F0.wireOp",EDGE,"E21.filletArc");var subQ1=sQuery(id+"F0.wireOp",EDGE,"E7");var subQ2=sQuery(id+"F0.wireOp",EDGE,"E6");var subQ3=sQuery(id+"F0.wireOp",EDGE,"E5");var subQ4=sQuery(id+"F0.wireOp",EDGE,"E4");var subQ5=sQuery(id+"F0.wireOp",EDGE,"E22.filletArc");var subQ6=sQuery(id+"F0.wireOp",EDGE,"E1.bottom");var subQ7=sQuery(id+"F0.wireOp",EDGE,"E1.right");var subQ8=sQuery(id+"F0.wireOp",EDGE,"E1.top");var subQ9=sQuery(id+"F0.wireOp",EDGE,"E1.left");var subQ10=sQuery(id+"F0.wireOp",EDGE,"E23.filletArc");var subQ11=sQuery(id+"F0.wireOp",EDGE,"E24.filletArc");Q0=makeQuery(id+"F2.boolean.opBoolean","SPLIT",FACE,{"disambiguationData":[TD([makeQuery(id+"F1.opExtrude","SWEPT_FACE",FACE,{"disambiguationData":[OSD([subQ6])]})])],"derivedFrom":makeQuery(id+"F1.opExtrude","CAP_FACE",FACE,{"disambiguationData":[OSD([subQ6,subQ8,subQ9,subQ7,subQ4,subQ3,subQ2,subQ1,subQ0,subQ5,subQ10,subQ11])],"isStart":true})});}
            var sketch = newSketch(context, id + "F16", { "sketchPlane" : qUnion([Q0])});
            skLineSegment(sketch, "E79", {"start": v(-33, 90) * mm, "end": v(-15, 108) * mm});
            skLineSegment(sketch, "E80", {"start": v(33, 90) * mm, "end": v(15, 108) * mm});
            skLineSegment(sketch, "E81", {"start": v(-15, 108) * mm, "end": v(-15, 120) * mm});
            skLineSegment(sketch, "E82", {"start": v(15, 108) * mm, "end": v(15, 120) * mm});
            skArc(sketch, "E83", {"start": v(15, 120) * mm, "mid": v(0, 135) * mm, "end": v(-15, 120) * mm});
            skCircle(sketch, "E84", {"center": v(0, 120) * mm, "radius": 6 * mm});
            skLineSegment(sketch, "E85", {"start": v(0, 120) * mm, "end": v(0, 90) * mm});
            skLineSegment(sketch, "E86", {"start": v(-80, 0) * mm, "end": v(80, 0) * mm});
            skArc(sketch, "E87.MirrorCS", {"start": v(15, -120) * mm, "mid": v(0, -135) * mm, "end": v(-15, -120) * mm});
            skLineSegment(sketch, "E88.MirrorCS", {"start": v(-15, -108) * mm, "end": v(-15, -120) * mm});
            skLineSegment(sketch, "E89.MirrorCS", {"start": v(15, -108) * mm, "end": v(15, -120) * mm});
            skLineSegment(sketch, "E90.MirrorCS", {"start": v(33, -90) * mm, "end": v(15, -108) * mm});
            skLineSegment(sketch, "E91.MirrorCS", {"start": v(-33, -90) * mm, "end": v(-15, -108) * mm});
            skCircle(sketch, "E92.MirrorC", {"center": v(0, -120) * mm, "radius": 6 * mm});
            skSolve(sketch);
        }
        {
            var Q0;
            Q0=makeQuery(id+"F16.imprint","IMPRINT",FACE,{"disambiguationData":[TD([[makeQuery(id+"F16.imprint","IMPRINT",EDGE,{"derivedFrom":makeQuery(id+"F1.opExtrude","CAP_EDGE",EDGE,{"disambiguationData":[OSD([sQuery(id+"F0.wireOp",EDGE,"E4")])],"isStart":true})}),-1.0]])]});
            var Q1;
            Q1=makeQuery(id+"F16.imprint","IMPRINT",FACE,{"disambiguationData":[TD([[makeQuery(id+"F16.imprint","IMPRINT",EDGE,{"derivedFrom":makeQuery(id+"F1.opExtrude","CAP_EDGE",EDGE,{"disambiguationData":[OSD([sQuery(id+"F0.wireOp",EDGE,"E6")])],"isStart":true})}),-1.0]])]});
            var Q2;
            Q2=makeQuery(id+"F16.imprint","IMPRINT",FACE,{"disambiguationData":[TD([[makeQuery(id+"F16.imprint","IMPRINT",EDGE,{"derivedFrom":sQuery(id+"F16.wireOp",EDGE,"E87.MirrorCS")}),-1.0]])]});
            var Q3;
            {var subQ3=sQuery(id+"F16.wireOp",EDGE,"E79");Q3=makeQuery(id+"F16.imprint","IMPRINT",FACE,{"disambiguationData":[TD([[makeQuery(id+"F16.imprint","IMPRINT",EDGE,{"derivedFrom":subQ3}),-1.0]])]});}
            var Q4;
            Q4=makeQuery(id+"F2.opExtrude","CAP_FACE",FACE,{"disambiguationData":[OSD([sQuery(id+"F0.wireOp",EDGE,"E12"),sQuery(id+"F0.wireOp",EDGE,"E13"),sQuery(id+"F0.wireOp",EDGE,"E14"),sQuery(id+"F0.wireOp",EDGE,"E15"),sQuery(id+"F0.wireOp",EDGE,"E17.filletArc"),sQuery(id+"F0.wireOp",EDGE,"E18.filletArc"),sQuery(id+"F0.wireOp",EDGE,"E19.filletArc"),sQuery(id+"F0.wireOp",EDGE,"E20.filletArc"),sQuery(id+"F0.wireOp",EDGE,"E25.0"),sQuery(id+"F0.wireOp",EDGE,"E25.1"),sQuery(id+"F0.wireOp",EDGE,"E25.2"),sQuery(id+"F0.wireOp",EDGE,"E25.3"),sQuery(id+"F0.wireOp",EDGE,"E25.4"),sQuery(id+"F0.wireOp",EDGE,"E25.5"),sQuery(id+"F0.wireOp",EDGE,"E25.6"),sQuery(id+"F0.wireOp",EDGE,"E25.7")])],"isStart":false});
            extrude(context, id + "F17", {"entities" : qUnion([Q0, Q1, Q2, Q3]), "endBound" : BoundingType.UP_TO_SURFACE, "depth" : 25 * mm, "endBoundEntityFace" : qUnion([Q4]), "offsetDistance" : 25 * mm});
        }
    });
